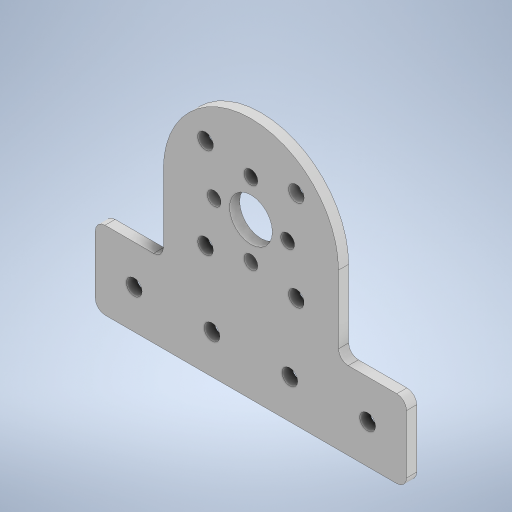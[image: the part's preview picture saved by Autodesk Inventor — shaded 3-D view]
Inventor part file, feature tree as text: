
AUTODESK INVENTOR PART (.ipt)
format: ipt  version: 2024 (Build 280153000, 153)  size: 311,296 bytes
history: native  units: in
note: dims shown in document units (in); Inventor stores cm internally (conversion verified against a paired STEP export)
features: sketch x2, hole x2, pattern_circular x2, extrude x1, fillet x1
ambient origin geometry x8: Origin, YZ Plane, XZ Plane, XY Plane, X Axis, Y Axis, Z Axis, Center Point
bodies: Solid1 (feature_tree)
feature tree (8):
  extrude  "Extrusion1"  Depth=0.13in TaperAngle=0.0deg
  fillet  "Fillet1"  Radius=0.203in
  sketch  "Sketch2"  dims[d11=0.203in d12=0.5in d13=0.5in d14=0.5in d15=0.5in d16=2.0in d17=1.0in d18=4.0in d19=2.0in d20=1.0in d21=1.0in d22=0.125in d25=1.125in d26=1.0in d27=0.9449in d28=1.65in d29=45.0deg d30=0.201in d31=0.75in d32=0.385in d33=0.25in d34=0.5635in d35=0.64in d36=0.8108in d37=1.5748in d38=360.0deg d41=0.177in d42=0.75in d43=0.375in d44=0.25in d45=0.5635in d46=0.64in d47=0.8108in d48=1.5748in d49=360.0deg]
  hole  "Hole1"  [1 undecoded]
  pattern_circular  "Circular Pattern1"  [2 undecoded]
  hole  "Hole2"  [1 undecoded]
  pattern_circular  "Circular Pattern2"  [2 undecoded]
  sketch  "Sketch1"  dims[d1=0.5512in d8=0.13in d9=0.0in d10=0.203in]
note: 6 required parameter values undecoded (feature->parameter linkage not recoverable at this tier; creation-order binding heuristic only, values carry confidence <= 0.55)
